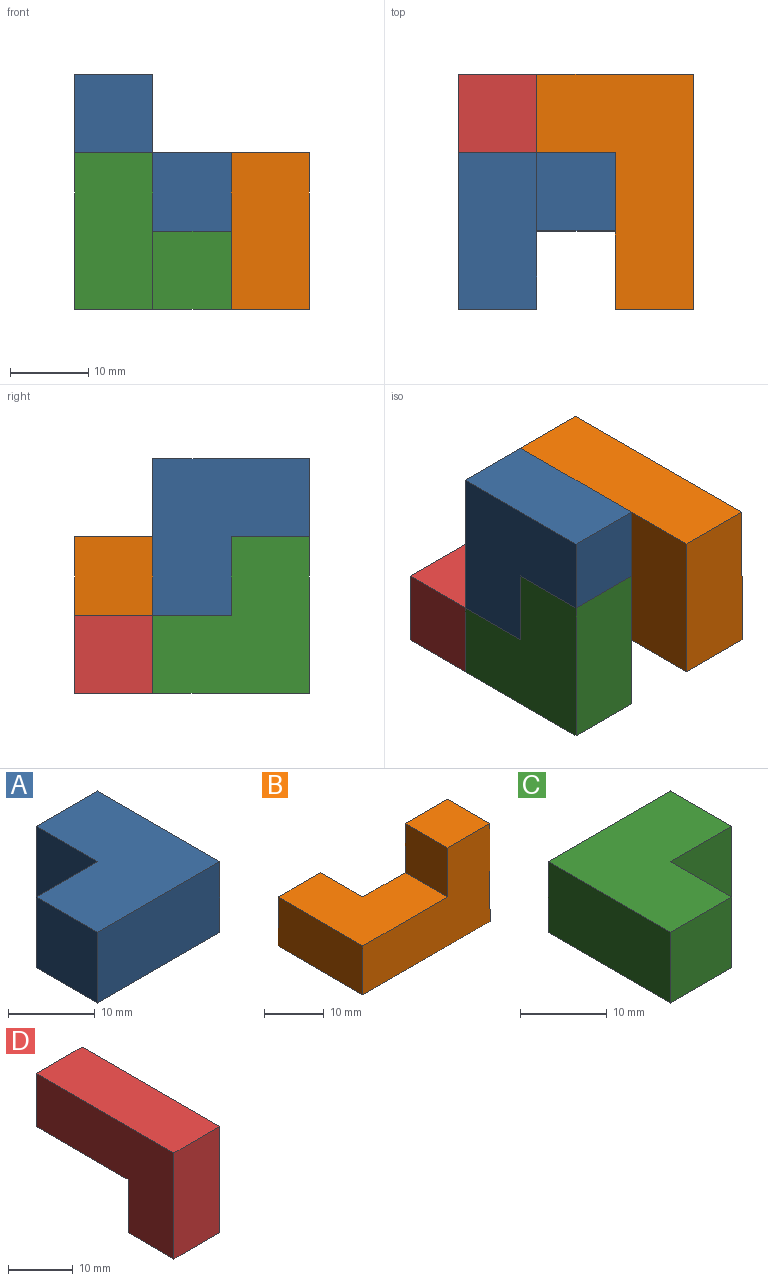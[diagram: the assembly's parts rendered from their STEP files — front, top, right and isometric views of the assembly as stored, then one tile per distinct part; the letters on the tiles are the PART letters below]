
ASSEMBLY  parts=4 mates=2
PART A: 10 faces, bbox 20x20x20 mm
  f0: plane 10x10mm, normal (-1,0,0), area 100mm2, adj f1,f6,f7,f8
  f1: plane 20x10mm, normal (0,-1,0), area 200mm2, adj f0,f3,f7,f8
  f2: plane 10x10mm, normal (0,0,-1), area 100mm2, adj f3,f4,f5,f9
  f3: plane 20x20mm, normal (1,0,0), area 300mm2, adj f1,f2,f4,f7,f8,f9
  f4: plane 20x10mm, normal (0,1,0), area 200mm2, adj f2,f3,f5,f7
  f5: plane 20x10mm, normal (-1,0,0), area 200mm2, adj f2,f4,f6,f7,f9
  f6: plane 10x10mm, normal (0,1,0), area 100mm2, adj f0,f5,f7,f8
  f7: plane 20x20mm, normal (0,0,1), area 300mm2, adj f0,f1,f3,f4,f5,f6
  f8: plane 20x10mm, normal (0,0,-1), area 200mm2, adj f0,f1,f3,f6,f9
  f9: plane 10x10mm, normal (0,-1,0), area 100mm2, adj f2,f3,f5,f8
PART B: 10 faces, bbox 30x20x20 mm
  f0: plane 20x20mm, normal (0,0,1), area 300mm2, adj f4,f5,f6,f7,f8,f9
  f1: plane 30x20mm, normal (0,0,-1), area 400mm2, adj f2,f5,f6,f7,f8,f9
  f2: plane 20x10mm, normal (1,0,0), area 200mm2, adj f1,f3,f7,f8
  f3: plane 10x10mm, normal (0,0,1), area 100mm2, adj f2,f4,f7,f8
  f4: plane 10x10mm, normal (-1,0,0), area 100mm2, adj f0,f3,f7,f8
  f5: plane 20x10mm, normal (-1,0,0), area 200mm2, adj f0,f1,f6,f7
  f6: plane 10x10mm, normal (0,1,0), area 100mm2, adj f0,f1,f5,f9
  f7: plane 30x20mm, normal (0,-1,0), area 400mm2, adj f0,f1,f2,f3,f4,f5
  f8: plane 20x20mm, normal (0,1,0), area 300mm2, adj f0,f1,f2,f3,f4,f9
  f9: plane 10x10mm, normal (1,0,0), area 100mm2, adj f0,f1,f6,f8
PART C: 10 faces, bbox 20x20x20 mm
  f0: plane 20x20mm, normal (0,0,1), area 300mm2, adj f3,f4,f6,f7,f8,f9
  f1: plane 10x10mm, normal (-1,0,0), area 100mm2, adj f2,f5,f7,f9
  f2: plane 10x10mm, normal (0,0,-1), area 100mm2, adj f1,f6,f7,f9
  f3: plane 10x10mm, normal (0,-1,0), area 100mm2, adj f0,f4,f5,f8
  f4: plane 20x10mm, normal (-1,0,0), area 200mm2, adj f0,f3,f5,f7
  f5: plane 20x10mm, normal (0,0,-1), area 200mm2, adj f1,f3,f4,f7,f8
  f6: plane 20x10mm, normal (1,0,0), area 200mm2, adj f0,f2,f7,f9
  f7: plane 20x20mm, normal (0,1,0), area 300mm2, adj f0,f1,f2,f4,f5,f6
  f8: plane 10x10mm, normal (1,0,0), area 100mm2, adj f0,f3,f5,f9
  f9: plane 20x10mm, normal (0,-1,0), area 200mm2, adj f0,f1,f2,f6,f8
PART D: 8 faces, bbox 10x30x20 mm
  f0: plane 30x20mm, normal (-1,0,0), area 400mm2, adj f1,f3,f4,f5,f6,f7
  f1: plane 10x10mm, normal (0,0,-1), area 100mm2, adj f0,f2,f5,f7
  f2: plane 30x20mm, normal (1,0,0), area 400mm2, adj f1,f3,f4,f5,f6,f7
  f3: plane 30x10mm, normal (0,0,1), area 300mm2, adj f0,f2,f4,f5
  f4: plane 10x10mm, normal (0,1,0), area 100mm2, adj f0,f2,f3,f6
  f5: plane 20x10mm, normal (0,-1,0), area 200mm2, adj f0,f1,f2,f3
  f6: plane 20x10mm, normal (0,0,-1), area 200mm2, adj f0,f2,f4,f7
  f7: plane 10x10mm, normal (0,1,0), area 100mm2, adj f0,f1,f2,f6
PLACE A rot(axis=(-0.58,-0.58,0.58),120deg) t=(-46.36,5.47,-46.86)mm
PLACE B rot(axis=(-0.58,-0.58,0.58),120deg) t=(-42.34,0.2,-28.14)mm
PLACE C rot(axis=(-0.58,-0.58,0.58),120deg) t=(-17.07,11.76,-48.14)mm
PLACE D rot(axis=(-0.58,0.58,0.58),120deg) t=(-16.36,28.88,-55.76)mm
MATE fastened C.f3 <-> A.f6  axis (0,0,1) through (-41.36,-9.53,-28.14)mm
MATE fastened A.f2 <-> B.f0  axis (1,0,0) through (-26.36,5.47,-33.14)mm
